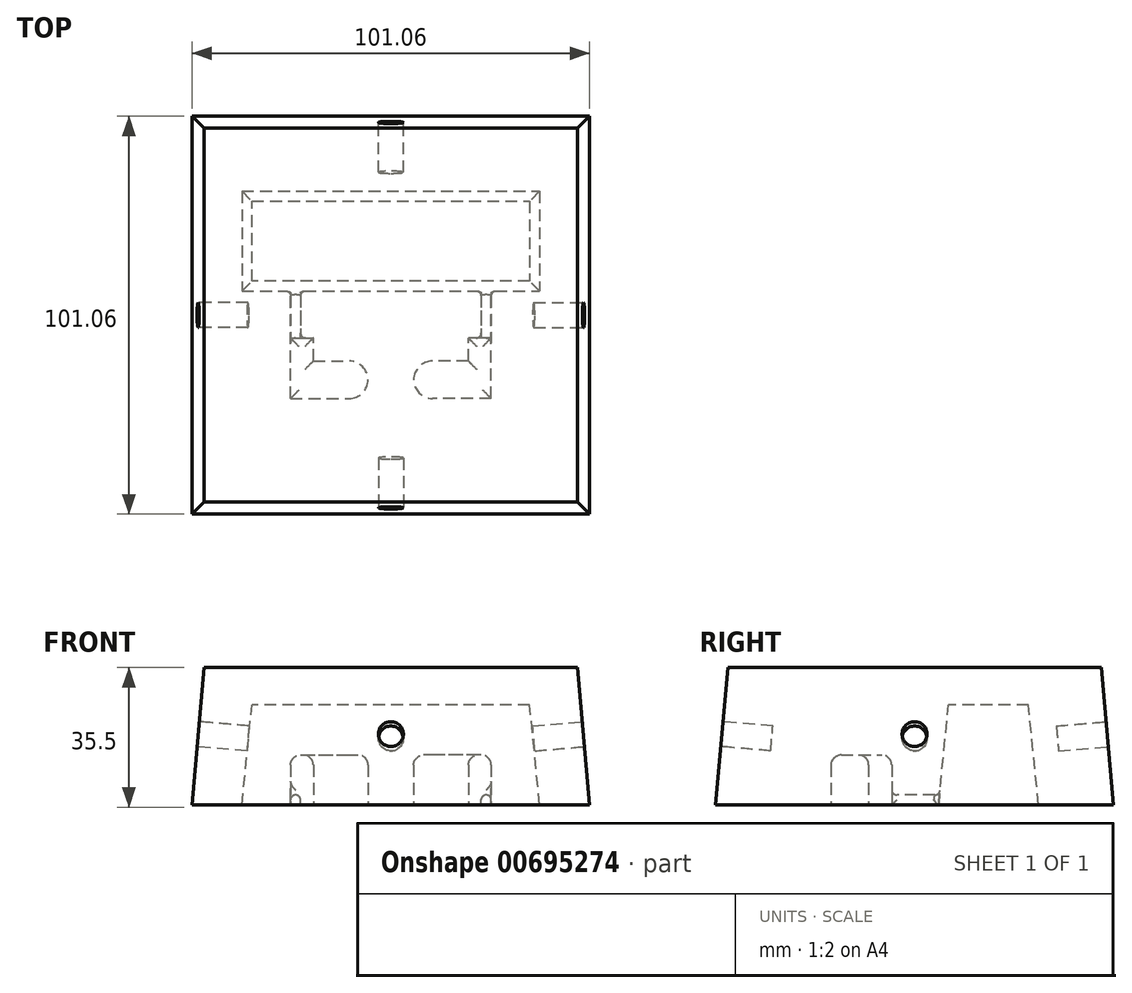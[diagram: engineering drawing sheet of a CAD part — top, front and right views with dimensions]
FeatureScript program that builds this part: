
annotation { "Feature Type Name" : "Feature", "Feature Type Description" : "" }
export const myFeature = defineFeature(function(context is Context, id is Id, definition is map)
    precondition{}
    {
        {
            var Q0;
            Q0=qCreatedBy(makeId("Top.planeOp"),FACE);
            var sketch = newSketch(context, id + "F0", { "sketchPlane" : qUnion([Q0])});
            skLineSegment(sketch, "E0.bottom", {"start": v(-50.8, -50.8) * mm, "end": v(50.8, -50.8) * mm});
            skLineSegment(sketch, "E0.top", {"start": v(-50.8, 50.8) * mm, "end": v(50.8, 50.8) * mm});
            skLineSegment(sketch, "E0.left", {"start": v(-50.8, -50.8) * mm, "end": v(-50.8, 50.8) * mm});
            skLineSegment(sketch, "E0.right", {"start": v(50.8, -50.8) * mm, "end": v(50.8, 50.8) * mm});
            skPoint(sketch, "E0.middle", {"position": v(0, 0) * mm});
            skSolve(sketch);
        }
        {
            var Q0;
            Q0=makeQuery(id+"F0.imprint","IMPRINT",FACE,{"disambiguationData":[TD([[makeQuery(id+"F0.imprint","IMPRINT",EDGE,{"derivedFrom":sQuery(id+"F0.wireOp",EDGE,"E0.bottom")}),1.0]])]});
            extrude(context, id + "F1", {"entities" : qUnion([Q0]), "depth" : 34.92 * mm, "offsetDistance" : 25.4 * mm});
        }
        {
            var Q0;
            Q0=makeQuery(id+"F1.opExtrude","CAP_FACE",FACE,{"disambiguationData":[OSD([sQuery(id+"F0.wireOp",EDGE,"E0.bottom"),sQuery(id+"F0.wireOp",EDGE,"E0.top"),sQuery(id+"F0.wireOp",EDGE,"E0.left"),sQuery(id+"F0.wireOp",EDGE,"E0.right")])],"isStart":false});
            chamfer(context, id + "F2", {"entities" : qUnion([Q0]), "chamferType" : ChamferType.OFFSET_ANGLE, "width" : 3.33 * mm, "oppositeDirection" : false, "angle" : 85 * degree, "tangentPropagation" : true});
        }
        {
            var Q0;
            Q0=makeQuery(id+"F2.opChamfer","BLEND_FACE",FACE,{"disambiguationData":[OSD([sQuery(id+"F0.wireOp",EDGE,"E0.top")])]});
            var sketch = newSketch(context, id + "F3", { "sketchPlane" : qUnion([Q0])});
            skLineSegment(sketch, "E1", {"start": v(50.53, -4.4) * mm, "end": v(-47.47, 30.65) * mm, "construction": true});
            skLineSegment(sketch, "E2", {"start": v(-50.53, -4.4) * mm, "end": v(47.47, 30.65) * mm, "construction": true});
            skCircle(sketch, "E3", {"center": v(0, 13.67) * mm, "radius": 3.18 * mm});
            skSolve(sketch);
        }
        {
            var Q0;
            Q0=makeQuery(id+"F3.imprint","IMPRINT",FACE,{"disambiguationData":[TD([[makeQuery(id+"F3.imprint","IMPRINT",EDGE,{"derivedFrom":sQuery(id+"F3.wireOp",EDGE,"E3")}),1.0]])]});
            extrude(context, id + "F4", {"entities" : qUnion([Q0]), "operationType" : NewBodyOperationType.REMOVE, "oppositeDirection" : true, "depth" : 12.7 * mm, "offsetDistance" : 25.4 * mm});
        }
        {
            var Q0;
            Q0=makeQuery(id+"F2.opChamfer","BLEND_FACE",FACE,{"disambiguationData":[OSD([sQuery(id+"F0.wireOp",EDGE,"E0.right")])]});
            var sketch = newSketch(context, id + "F5", { "sketchPlane" : qUnion([Q0])});
            skLineSegment(sketch, "E4", {"start": v(50.53, -4.4) * mm, "end": v(-47.47, 30.65) * mm, "construction": true});
            skLineSegment(sketch, "E5", {"start": v(-50.53, -4.4) * mm, "end": v(47.47, 30.65) * mm, "construction": true});
            skCircle(sketch, "E6", {"center": v(0, 13.67) * mm, "radius": 3.18 * mm});
            skSolve(sketch);
        }
        {
            var Q0;
            Q0=makeQuery(id+"F5.imprint","IMPRINT",FACE,{"disambiguationData":[TD([[makeQuery(id+"F5.imprint","IMPRINT",EDGE,{"derivedFrom":sQuery(id+"F5.wireOp",EDGE,"E6")}),1.0]])]});
            extrude(context, id + "F6", {"entities" : qUnion([Q0]), "operationType" : NewBodyOperationType.REMOVE, "oppositeDirection" : true, "depth" : 12.7 * mm, "offsetDistance" : 25.4 * mm});
        }
        {
            var Q0;
            Q0=makeQuery(id+"F2.opChamfer","BLEND_FACE",FACE,{"disambiguationData":[OSD([sQuery(id+"F0.wireOp",EDGE,"E0.bottom")])]});
            var sketch = newSketch(context, id + "F7", { "sketchPlane" : qUnion([Q0])});
            skLineSegment(sketch, "E7", {"start": v(50.53, -4.4) * mm, "end": v(-47.47, 30.65) * mm, "construction": true});
            skLineSegment(sketch, "E8", {"start": v(-50.53, -4.4) * mm, "end": v(47.47, 30.65) * mm, "construction": true});
            skCircle(sketch, "E9", {"center": v(0, 13.67) * mm, "radius": 3.18 * mm});
            skSolve(sketch);
        }
        {
            var Q0;
            Q0=makeQuery(id+"F7.imprint","IMPRINT",FACE,{"disambiguationData":[TD([[makeQuery(id+"F7.imprint","IMPRINT",EDGE,{"derivedFrom":sQuery(id+"F7.wireOp",EDGE,"E9")}),1.0]])]});
            extrude(context, id + "F8", {"entities" : qUnion([Q0]), "operationType" : NewBodyOperationType.REMOVE, "oppositeDirection" : true, "depth" : 12.7 * mm, "offsetDistance" : 25.4 * mm});
        }
        {
            var Q0;
            Q0=makeQuery(id+"F2.opChamfer","BLEND_FACE",FACE,{"disambiguationData":[OSD([sQuery(id+"F0.wireOp",EDGE,"E0.left")])]});
            var sketch = newSketch(context, id + "F9", { "sketchPlane" : qUnion([Q0])});
            skLineSegment(sketch, "E10", {"start": v(50.53, -4.4) * mm, "end": v(-47.47, 30.65) * mm, "construction": true});
            skLineSegment(sketch, "E11", {"start": v(47.47, 30.65) * mm, "end": v(-50.53, -4.4) * mm, "construction": true});
            skCircle(sketch, "E12", {"center": v(0, 13.67) * mm, "radius": 3.18 * mm});
            skSolve(sketch);
        }
        {
            var Q0;
            Q0=makeQuery(id+"F9.imprint","IMPRINT",FACE,{"disambiguationData":[TD([[makeQuery(id+"F9.imprint","IMPRINT",EDGE,{"derivedFrom":sQuery(id+"F9.wireOp",EDGE,"E12")}),1.0]])]});
            extrude(context, id + "F10", {"entities" : qUnion([Q0]), "operationType" : NewBodyOperationType.REMOVE, "oppositeDirection" : true, "depth" : 12.7 * mm, "offsetDistance" : 25.4 * mm});
        }
        {
            var Q0;
            Q0=makeQuery(id+"F1.opExtrude","CAP_FACE",FACE,{"disambiguationData":[OSD([sQuery(id+"F0.wireOp",EDGE,"E0.bottom"),sQuery(id+"F0.wireOp",EDGE,"E0.top"),sQuery(id+"F0.wireOp",EDGE,"E0.left"),sQuery(id+"F0.wireOp",EDGE,"E0.right")])],"isStart":true});
            var sketch = newSketch(context, id + "F11", { "sketchPlane" : qUnion([Q0])});
            skLineSegment(sketch, "E13.bottom", {"start": v(-50.53, -50.53) * mm, "end": v(-37.83, -50.53) * mm, "construction": true});
            skLineSegment(sketch, "E13.top", {"start": v(-50.53, -31.48) * mm, "end": v(-37.83, -31.48) * mm, "construction": true});
            skLineSegment(sketch, "E13.left", {"start": v(-50.53, -50.53) * mm, "end": v(-50.53, -31.48) * mm, "construction": true});
            skLineSegment(sketch, "E13.right", {"start": v(-37.83, -50.53) * mm, "end": v(-37.83, -31.48) * mm, "construction": true});
            skLineSegment(sketch, "E14.bottom", {"start": v(50.53, -50.53) * mm, "end": v(37.83, -50.53) * mm, "construction": true});
            skLineSegment(sketch, "E14.top", {"start": v(50.53, -31.48) * mm, "end": v(37.83, -31.48) * mm, "construction": true});
            skLineSegment(sketch, "E14.left", {"start": v(50.53, -50.53) * mm, "end": v(50.53, -31.48) * mm, "construction": true});
            skLineSegment(sketch, "E14.right", {"start": v(37.83, -50.53) * mm, "end": v(37.83, -31.48) * mm, "construction": true});
            skLineSegment(sketch, "E15.left", {"start": v(-37.83, -31.48) * mm, "end": v(-37.83, -31.48) * mm});
            skLineSegment(sketch, "E15.right", {"start": v(37.83, -31.48) * mm, "end": v(37.83, -31.48) * mm});
            skLineSegment(sketch, "E16.bottom", {"start": v(-37.83, -31.48) * mm, "end": v(37.83, -31.48) * mm});
            skLineSegment(sketch, "E16.top", {"start": v(-37.83, -6.08) * mm, "end": v(37.83, -6.08) * mm});
            skLineSegment(sketch, "E16.left", {"start": v(-37.83, -31.48) * mm, "end": v(-37.83, -6.08) * mm});
            skLineSegment(sketch, "E16.right", {"start": v(37.83, -31.48) * mm, "end": v(37.83, -6.08) * mm});
            skSolve(sketch);
        }
        {
            var Q0;
            Q0=makeQuery(id+"F11.imprint","IMPRINT",FACE,{"disambiguationData":[TD([[makeQuery(id+"F11.imprint","IMPRINT",EDGE,{"derivedFrom":sQuery(id+"F11.wireOp",EDGE,"E16.bottom")}),1.0]])]});
            extrude(context, id + "F12", {"entities" : qUnion([Q0]), "operationType" : NewBodyOperationType.REMOVE, "oppositeDirection" : true, "depth" : 25.4 * mm, "offsetDistance" : 25.4 * mm});
        }
        {
            var Q0;
            Q0=makeQuery(id+"F12.boolean.opBoolean","COPY",FACE,{"derivedFrom":makeQuery(id+"F12.opExtrude","CAP_FACE",FACE,{"disambiguationData":[OSD([sQuery(id+"F11.wireOp",EDGE,"E16.bottom"),sQuery(id+"F11.wireOp",EDGE,"E16.top"),sQuery(id+"F11.wireOp",EDGE,"E16.left"),sQuery(id+"F11.wireOp",EDGE,"E16.right")])],"isStart":false})});
            chamfer(context, id + "F13", {"entities" : qUnion([Q0]), "chamferType" : ChamferType.TWO_OFFSETS, "width1" : 2.54 * mm, "oppositeDirection" : false, "width2" : 25.4 * mm, "tangentPropagation" : true});
        }
        {
            var Q0;
            Q0=makeQuery(id+"F1.opExtrude","CAP_FACE",FACE,{"disambiguationData":[OSD([sQuery(id+"F0.wireOp",EDGE,"E0.bottom"),sQuery(id+"F0.wireOp",EDGE,"E0.top"),sQuery(id+"F0.wireOp",EDGE,"E0.left"),sQuery(id+"F0.wireOp",EDGE,"E0.right")])],"isStart":true});
            var sketch = newSketch(context, id + "F14", { "sketchPlane" : qUnion([Q0])});
            skLineSegment(sketch, "E17", {"start": v(0, 50.53) * mm, "end": v(0, -6.08) * mm, "construction": true});
            skArc(sketch, "E18", {"start": v(-10.55, 11.66) * mm, "mid": v(-5.8, 16.42) * mm, "end": v(-10.55, 21.19) * mm});
            skLineSegment(sketch, "E19.bottom", {"start": v(-25.49, 21.19) * mm, "end": v(-10.55, 21.19) * mm});
            skLineSegment(sketch, "E19.top", {"start": v(-19.7, 11.66) * mm, "end": v(-10.55, 11.66) * mm});
            skLineSegment(sketch, "E19.left", {"start": v(-25.49, 21.19) * mm, "end": v(-25.49, 11.66) * mm});
            skLineSegment(sketch, "E19.right", {"start": v(-10.55, 21.19) * mm, "end": v(-10.55, 21.19) * mm});
            skLineSegment(sketch, "E20.bottom", {"start": v(-25.49, 21.19) * mm, "end": v(-19.7, 21.19) * mm});
            skLineSegment(sketch, "E20.top", {"start": v(-25.49, 5.81) * mm, "end": v(-19.7, 5.81) * mm});
            skLineSegment(sketch, "E20.left", {"start": v(-25.49, 21.19) * mm, "end": v(-25.49, 5.81) * mm});
            skLineSegment(sketch, "E20.right", {"start": v(-19.7, 11.66) * mm, "end": v(-19.7, 5.81) * mm});
            skLineSegment(sketch, "E21.MirrorCS", {"start": v(10.55, 21.19) * mm, "end": v(10.55, 21.19) * mm});
            skLineSegment(sketch, "E22.MirrorCS", {"start": v(25.49, 21.19) * mm, "end": v(25.49, 11.66) * mm});
            skLineSegment(sketch, "E23.MirrorCS", {"start": v(19.7, 11.66) * mm, "end": v(19.7, 5.81) * mm});
            skLineSegment(sketch, "E24.MirrorCS", {"start": v(25.49, 21.19) * mm, "end": v(25.49, 5.81) * mm});
            skLineSegment(sketch, "E25.MirrorCS", {"start": v(25.49, 5.81) * mm, "end": v(19.7, 5.81) * mm});
            skLineSegment(sketch, "E26.MirrorCS", {"start": v(25.49, 21.19) * mm, "end": v(19.7, 21.19) * mm});
            skLineSegment(sketch, "E27.MirrorCS", {"start": v(25.49, 21.19) * mm, "end": v(10.55, 21.19) * mm});
            skLineSegment(sketch, "E28.MirrorCS", {"start": v(19.7, 11.66) * mm, "end": v(10.55, 11.66) * mm});
            skArc(sketch, "E29.MirrorCS", {"start": v(10.55, 11.66) * mm, "mid": v(5.8, 16.42) * mm, "end": v(10.55, 21.19) * mm});
            skSolve(sketch);
        }
        {
            var Q0;
            Q0=qSketchRegion(id+"F14",true);
            extrude(context, id + "F15", {"entities" : qUnion([Q0]), "operationType" : NewBodyOperationType.REMOVE, "oppositeDirection" : true, "depth" : 12.7 * mm, "offsetDistance" : 25.4 * mm});
        }
        {
            var Q0;
            Q0=makeQuery(id+"F15.boolean.opBoolean","COPY",FACE,{"derivedFrom":makeQuery(id+"F15.opExtrude","CAP_FACE",FACE,{"disambiguationData":[OSD([sQuery(id+"F14.wireOp",EDGE,"E18"),sQuery(id+"F14.wireOp",EDGE,"E19.bottom"),sQuery(id+"F14.wireOp",EDGE,"E19.top"),sQuery(id+"F14.wireOp",EDGE,"E19.right"),sQuery(id+"F14.wireOp",EDGE,"E20.bottom"),sQuery(id+"F14.wireOp",EDGE,"E20.top"),sQuery(id+"F14.wireOp",EDGE,"E20.left"),sQuery(id+"F14.wireOp",EDGE,"E20.right")])],"isStart":false})});
            var Q1;
            Q1=makeQuery(id+"F15.boolean.opBoolean","COPY",FACE,{"derivedFrom":makeQuery(id+"F15.opExtrude","CAP_FACE",FACE,{"disambiguationData":[OSD([sQuery(id+"F14.wireOp",EDGE,"E21.MirrorCS"),sQuery(id+"F14.wireOp",EDGE,"E23.MirrorCS"),sQuery(id+"F14.wireOp",EDGE,"E24.MirrorCS"),sQuery(id+"F14.wireOp",EDGE,"E25.MirrorCS"),sQuery(id+"F14.wireOp",EDGE,"E27.MirrorCS"),sQuery(id+"F14.wireOp",EDGE,"E28.MirrorCS"),sQuery(id+"F14.wireOp",EDGE,"E29.MirrorCS")])],"isStart":false})});
            fillet(context, id + "F16", {"entities" : qUnion([Q0, Q1]), "radius" : 2.54 * mm, "tangentPropagation" : true, "allowEdgeOverflow" : false});
        }
        {
            var Q0;
            Q0=makeQuery(id+"F15.boolean.opBoolean","COPY",FACE,{"derivedFrom":makeQuery(id+"F15.opExtrude","SWEPT_FACE",FACE,{"disambiguationData":[OSD([sQuery(id+"F14.wireOp",EDGE,"E20.top")])]})});
            var sketch = newSketch(context, id + "F17", { "sketchPlane" : qUnion([Q0])});
            skLineSegment(sketch, "E30.bottom", {"start": v(-25.49, 0) * mm, "end": v(-22.95, 0) * mm});
            skLineSegment(sketch, "E30.top", {"start": v(-25.49, 2.54) * mm, "end": v(-22.95, 2.54) * mm});
            skLineSegment(sketch, "E30.left", {"start": v(-25.49, 0) * mm, "end": v(-25.49, 2.54) * mm});
            skLineSegment(sketch, "E30.right", {"start": v(-22.95, 0) * mm, "end": v(-22.95, 2.54) * mm});
            skSolve(sketch);
        }
        {
            var Q0;
            Q0=makeQuery(id+"F17.imprint","IMPRINT",FACE,{"disambiguationData":[TD([[makeQuery(id+"F17.imprint","IMPRINT",EDGE,{"derivedFrom":sQuery(id+"F17.wireOp",EDGE,"E30.bottom")}),1.0]])]});
            var Q1;
            Q1=makeQuery(id+"F13.opChamfer","BLEND_FACE",FACE,{"disambiguationData":[OSD([sQuery(id+"F11.wireOp",EDGE,"E16.top")])]});
            extrude(context, id + "F18", {"entities" : qUnion([Q0]), "operationType" : NewBodyOperationType.REMOVE, "endBound" : BoundingType.UP_TO_SURFACE, "oppositeDirection" : true, "depth" : 25.4 * mm, "endBoundEntityFace" : qUnion([Q1]), "offsetDistance" : 25.4 * mm});
        }
        {
            var Q0;
            Q0=makeQuery(id+"F15.boolean.opBoolean","COPY",FACE,{"derivedFrom":makeQuery(id+"F15.opExtrude","SWEPT_FACE",FACE,{"disambiguationData":[OSD([sQuery(id+"F14.wireOp",EDGE,"E25.MirrorCS")])]})});
            var sketch = newSketch(context, id + "F19", { "sketchPlane" : qUnion([Q0])});
            skLineSegment(sketch, "E31.bottom", {"start": v(25.49, 0) * mm, "end": v(22.95, 0) * mm});
            skLineSegment(sketch, "E31.top", {"start": v(25.49, 2.54) * mm, "end": v(22.95, 2.54) * mm});
            skLineSegment(sketch, "E31.left", {"start": v(25.49, 0) * mm, "end": v(25.49, 2.54) * mm});
            skLineSegment(sketch, "E31.right", {"start": v(22.95, 0) * mm, "end": v(22.95, 2.54) * mm});
            skSolve(sketch);
        }
        {
            var Q0;
            Q0=makeQuery(id+"F19.imprint","IMPRINT",FACE,{"disambiguationData":[TD([[makeQuery(id+"F19.imprint","IMPRINT",EDGE,{"derivedFrom":sQuery(id+"F19.wireOp",EDGE,"E31.bottom")}),-1.0]])]});
            var Q1;
            Q1=makeQuery(id+"F13.opChamfer","BLEND_FACE",FACE,{"disambiguationData":[OSD([sQuery(id+"F11.wireOp",EDGE,"E16.top")])]});
            extrude(context, id + "F20", {"entities" : qUnion([Q0]), "operationType" : NewBodyOperationType.REMOVE, "endBound" : BoundingType.UP_TO_SURFACE, "oppositeDirection" : true, "depth" : 25.4 * mm, "endBoundEntityFace" : qUnion([Q1]), "offsetDistance" : 25.4 * mm});
        }
        {
            var Q0;
            Q0=makeQuery(id+"F18.boolean.opBoolean","COPY",FACE,{"derivedFrom":makeQuery(id+"F18.opExtrude","SWEPT_FACE",FACE,{"disambiguationData":[OSD([sQuery(id+"F17.wireOp",EDGE,"E30.top")])]})});
            fillet(context, id + "F21", {"entities" : qUnion([Q0]), "radius" : 1.27 * mm, "tangentPropagation" : true, "allowEdgeOverflow" : false});
        }
        {
            var Q0;
            Q0=makeQuery(id+"F20.boolean.opBoolean","COPY",FACE,{"derivedFrom":makeQuery(id+"F20.opExtrude","SWEPT_FACE",FACE,{"disambiguationData":[OSD([sQuery(id+"F19.wireOp",EDGE,"E31.top")])]})});
            fillet(context, id + "F22", {"entities" : qUnion([Q0]), "radius" : 1.27 * mm, "tangentPropagation" : true, "allowEdgeOverflow" : false});
        }
    });
